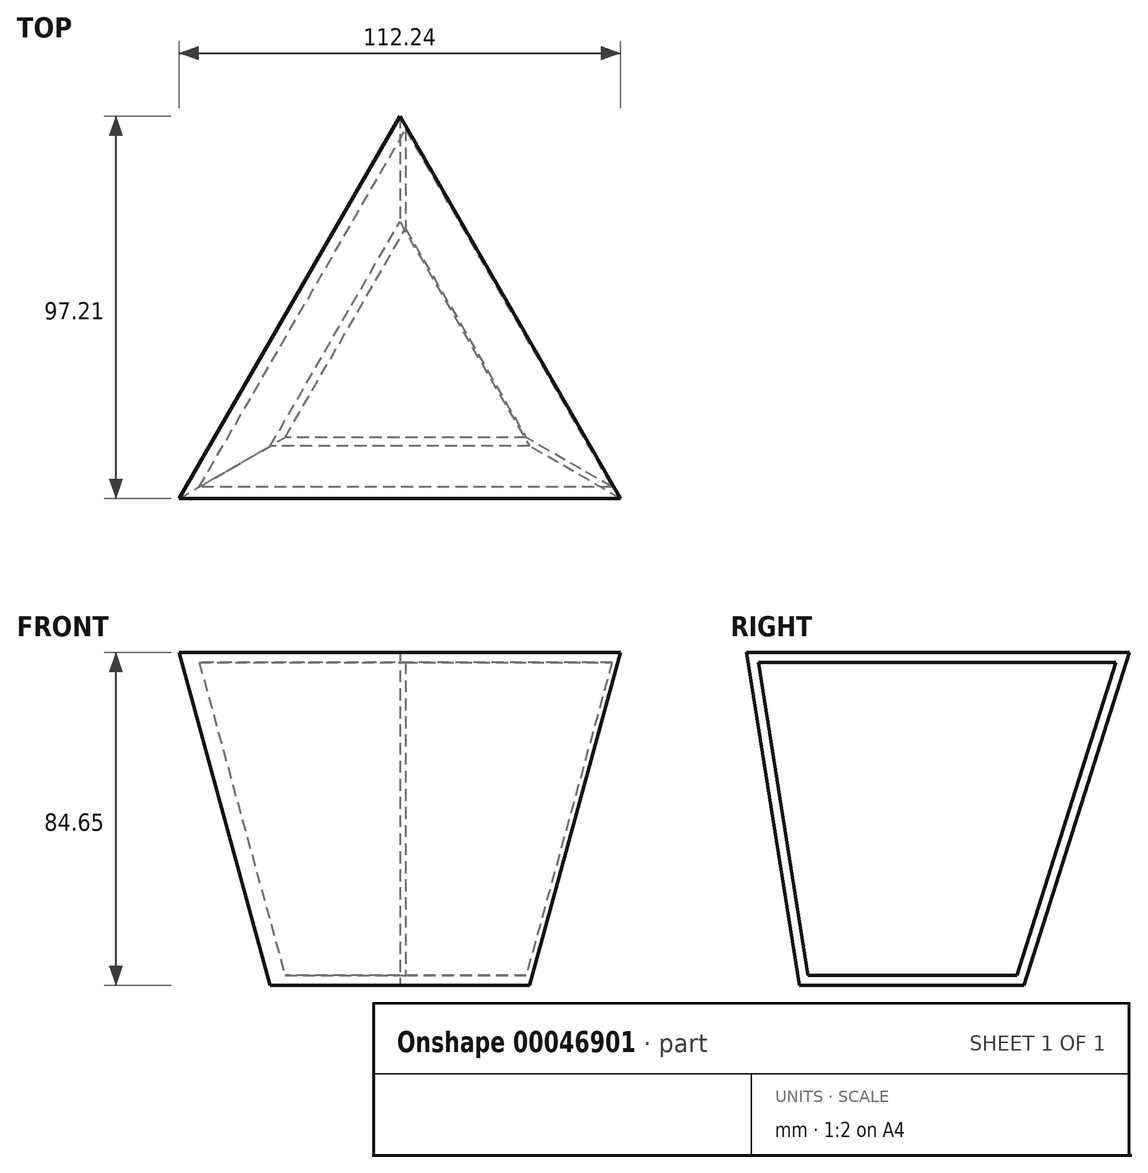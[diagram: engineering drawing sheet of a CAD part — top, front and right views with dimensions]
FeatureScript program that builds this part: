
annotation { "Feature Type Name" : "Feature", "Feature Type Description" : "" }
export const myFeature = defineFeature(function(context is Context, id is Id, definition is map)
    precondition{}
    {
        {
            var Q0;
            Q0=qCreatedBy(makeId("Top.planeOp"),FACE);
            var sketch = newSketch(context, id + "F0", { "sketchPlane" : qUnion([Q0])});
            skCircle(sketch, "E0.cCircle", {"center": v(0, 0) * mm, "radius": 38 * mm, "construction": true});
            skLineSegment(sketch, "E0.0", {"start": v(0, 38) * mm, "end": v(32.9, -19) * mm});
            skLineSegment(sketch, "E0.1", {"start": v(32.9, -19) * mm, "end": v(-32.9, -19) * mm});
            skLineSegment(sketch, "E0.2", {"start": v(-32.9, -19) * mm, "end": v(0, 38) * mm});
            skCircle(sketch, "E1.cCircle", {"center": v(0, 0) * mm, "radius": 64.7 * mm, "construction": true});
            skLineSegment(sketch, "E1.0", {"start": v(0, 64.7) * mm, "end": v(56.03, -32.35) * mm});
            skLineSegment(sketch, "E1.1", {"start": v(56.03, -32.35) * mm, "end": v(-56.03, -32.35) * mm});
            skLineSegment(sketch, "E1.2", {"start": v(-56.03, -32.35) * mm, "end": v(0, 64.7) * mm});
            skSolve(sketch);
        }
        {
            var Q0;
            Q0=makeQuery(id+"F0.imprint","IMPRINT",FACE,{"disambiguationData":[TD([[makeQuery(id+"F0.imprint","IMPRINT",EDGE,{"derivedFrom":sQuery(id+"F0.wireOp",EDGE,"E0.0")}),-1.0]])]});
            extrude(context, id + "F1", {"entities" : qUnion([Q0]), "depth" : 84.65 * mm, "hasDraft" : true, "draftAngle" : 9 * degree});
        }
        {
            var Q0;
            Q0=makeQuery(id+"F1.opExtrude","SWEPT_FACE",FACE,{"disambiguationData":[OSD([sQuery(id+"F0.wireOp",EDGE,"E0.0")])]});
            shell(context, id + "F2", {"entities" : qUnion([Q0]), "thickness" : 2.54 * mm});
        }
    });
